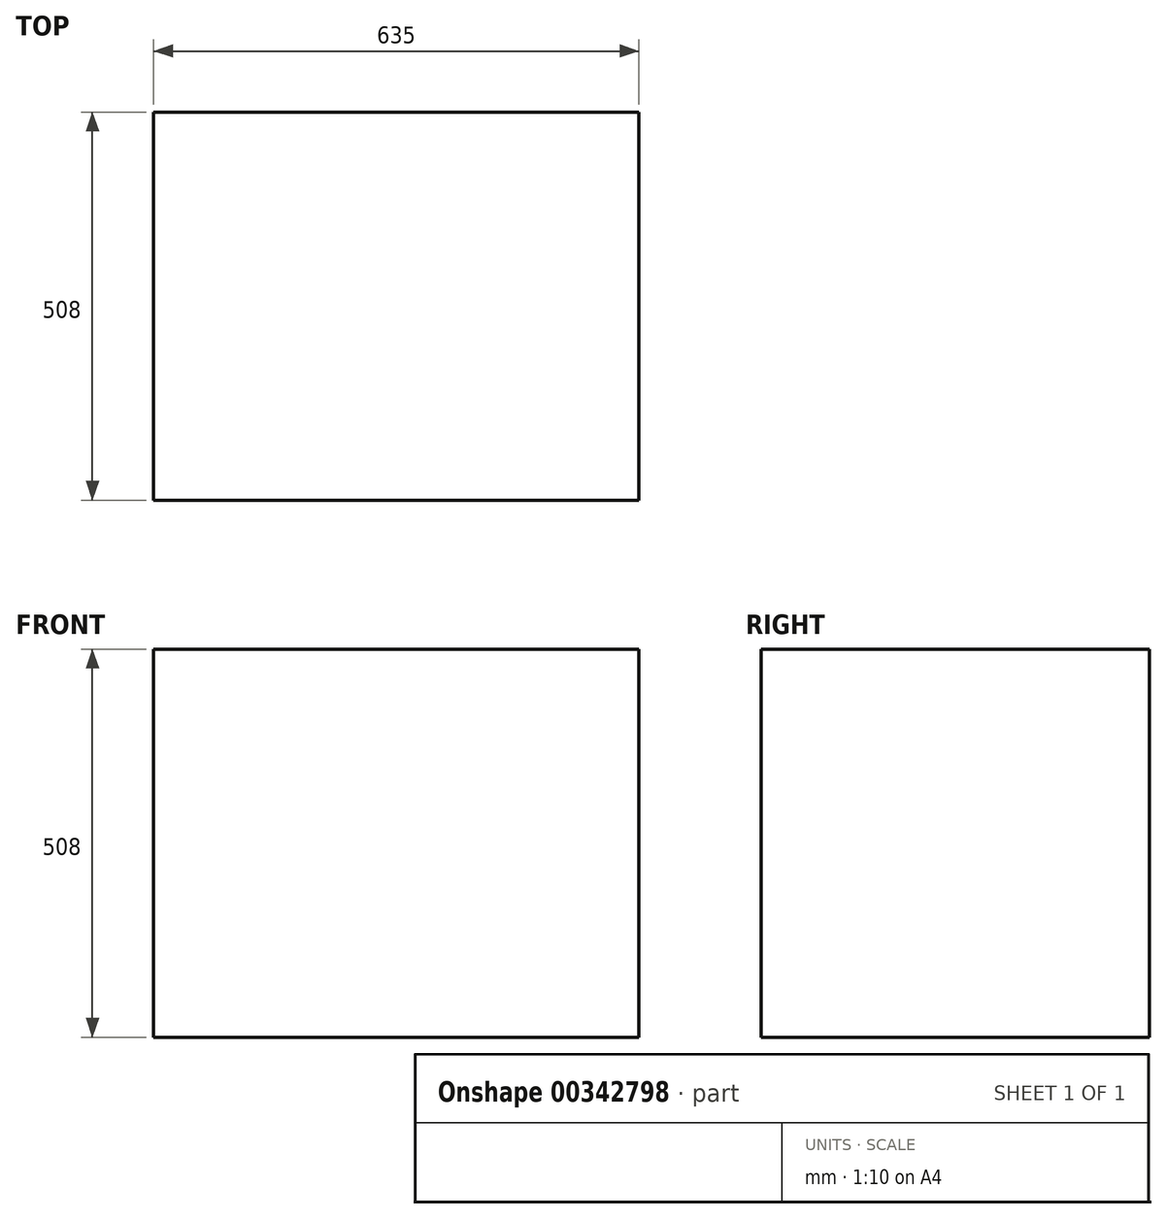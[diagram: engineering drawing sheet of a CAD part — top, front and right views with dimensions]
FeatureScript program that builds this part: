
annotation { "Feature Type Name" : "Feature", "Feature Type Description" : "" }
export const myFeature = defineFeature(function(context is Context, id is Id, definition is map)
    precondition{}
    {
        {
            var Q0;
            Q0=qCreatedBy(makeId("Front.planeOp"),FACE);
            var sketch = newSketch(context, id + "F0", { "sketchPlane" : qUnion([Q0])});
            skLineSegment(sketch, "E0.bottom", {"start": v(0, 0) * mm, "end": v(635, 0) * mm});
            skLineSegment(sketch, "E0.top", {"start": v(0, 508) * mm, "end": v(635, 508) * mm});
            skLineSegment(sketch, "E0.left", {"start": v(0, 0) * mm, "end": v(0, 508) * mm});
            skLineSegment(sketch, "E0.right", {"start": v(635, 0) * mm, "end": v(635, 508) * mm});
            skSolve(sketch);
        }
        {
            var Q0;
            Q0 = qSketchRegion(id + "F0", true);
            extrude(context, id + "F1", {"entities" : qUnion([Q0]), "depth" : 508 * mm});
        }
    });
